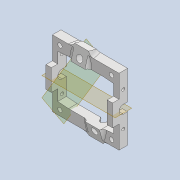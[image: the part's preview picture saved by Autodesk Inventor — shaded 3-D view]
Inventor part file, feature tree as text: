
AUTODESK INVENTOR PART (.ipt)
format: ipt  version: 2020 (Build 240168000, 168)  size: 697,856 bytes
history: native  units: mm
features: reference x17, projected_geometry x17, extrude x15, sketch x15, other x7, plane x4, fillet x4, thicken_offset x4, mirror x2, chamfer x2
ambient origin geometry x8: Origin, YZ Plane, XZ Plane, XY Plane, X Axis, Y Axis, Z Axis, Center Point
bodies: Solid1 (feature_tree)
feature tree (87):
  extrude  "Extrusion1"  Depth=21.0mm
  extrude  "Extrusion2"  Depth=2.5mm
  extrude  "Extrusion3"  Depth=4.0mm TaperAngle=0.0deg
  extrude  "Extrusion4"  Depth=10.0mm TaperAngle=0.0deg
  extrude  "Extrusion5"  Depth=10.0mm TaperAngle=0.0deg
  extrude  "Extrusion6"  Depth=4.0mm
  extrude  "Extrusion7"  Depth=10.0mm
  plane  "Work Plane1"
  sketch  "Sketch8"  dims[d19=10.0mm d20=50.0mm d21=0.0mm]
  plane  "Work Plane2"
  extrude  "Extrusion8"  Depth=10.0mm TaperAngle=0.0deg
  plane  "Work Plane3"
  mirror  "Mirror1"
  extrude  "Extrusion9"  Depth=14.0mm
  sketch  "Sketch10"  dims[d25=12.0mm d26=50.0mm d27=0.0mm]
  plane  "Work Plane4"
  extrude  "Extrusion11"  Depth=50.0mm TaperAngle=0.0deg
  mirror  "Mirror2"
  extrude  "Extrusion12"  Depth=24.0mm
  chamfer  "Chamfer1"  Distance=5.0mm
  fillet  "Fillet1"  Radius=5.0mm
  extrude  "Extrusion13"  Depth=0.4mm
  chamfer  "Chamfer2"  Distance=5.0mm
  fillet  "Fillet2"  Radius=0.4mm
  thicken_offset  "Thicken1"
  thicken_offset  "Thicken2"
  thicken_offset  "Thicken3"
  thicken_offset  "Thicken4"
  extrude  "Extrusion14"  Depth=4.0mm TaperAngle=0.0deg
  extrude  "Extrusion15"  Depth=2.5mm
  fillet  "Fillet3"  Radius=3.85mm
  fillet  "Fillet4"  Radius=2.5mm
  extrude  "Extrusion16"  Depth=3.0mm
  sketch  "Sketch1"  dims[d0=26.0mm d1=21.0mm]
  reference  "Reference1"
  reference  "Reference2"
  reference  "Reference3"
  reference  "Reference4"
  reference  "Reference5"
  reference  "Reference6"
  reference  "Reference7"
  reference  "Reference8"
  sketch  "Sketch2"  dims[d2=5.0mm d3=2.5mm]
  reference  "Reference9"
  reference  "Reference10"
  sketch  "Sketch3"  dims[d4=4.0mm d5=0.0mm d6=4.0mm d7=0.0mm]
  projected_geometry  "Projected Loop1"
  reference  "Reference11"
  sketch  "Sketch4"  dims[d8=10.0mm d9=4.0mm d10=0.0mm]
  reference  "Reference12"
  sketch  "Sketch5"  dims[d11=10.0mm d12=4.0mm d13=0.0mm]
  reference  "Reference13"
  sketch  "Sketch6"  dims[d14=5.0mm d15=4.0mm]
  projected_geometry  "Projected Loop2"
  sketch  "Sketch7"  dims[d16=50.0mm d17=0.0mm d18=10.0mm]
  projected_geometry  "Projected Loop3"
  projected_geometry  "Projected Loop4"
  projected_geometry  "Projected Loop5"
  reference  "Reference14"
  sketch  "Sketch9"  dims[d22=50.0mm d23=0.0mm d24=14.0mm]
  projected_geometry  "Projected Loop6"
  projected_geometry  "Projected Loop7"
  projected_geometry  "Projected Loop8"
  projected_geometry  "Projected Loop9"
  projected_geometry  "Projected Loop10"
  reference  "Reference15"
  projected_geometry  "Projected Loop11"
  sketch  "Sketch11"  dims[d28=26.0mm d29=24.0mm]
  reference  "Reference16"
  projected_geometry  "Projected Loop12"
  sketch  "Sketch12"  dims[d30=2.0mm]
  projected_geometry  "Projected Loop13"
  reference  "Reference17"
  sketch  "Sketch13"  dims[d31=2.0mm]
  projected_geometry  "Projected Loop14"
  sketch  "Sketch14"  dims[d32=2.0mm]
  projected_geometry  "Projected Loop15"
  sketch  "Sketch15"  dims[d33=2.0mm d34=5.0mm d35=0.0mm d37=5.0mm d38=0.4mm d39=5.0mm d42=0.4mm d43=4.0mm d44=0.0mm d45=2.5mm d46=3.85mm d47=2.5mm d48=3.0mm d49=7.0mm d50=0.0mm d51=0.5mm d52=2.0mm d53=45.0deg d54=0.2mm d55=2.5mm d56=3.85mm d57=3.0mm d58=7.0mm d59=0.0mm d60=0.5mm d61=2.0mm d62=45.0deg d63=0.2mm d64=8.25mm d65=9.0mm d66=6.0mm d67=6.0mm d68=1.5mm d69=1.5mm d70=0.75mm d71=0.75mm d72=6.5mm d73=1.5mm d74=7.0mm d75=0.0mm d76=6.5mm d77=1.5mm d78=7.0mm d79=0.0mm d80=3.0mm d81=2.0mm d82=5.0mm d83=5.0mm d84=1.4mm d85=1.4mm d86=7.0mm d87=0.0mm]
  projected_geometry  "Projected Loop16"
  projected_geometry  "Projected Loop17"
  parser-record x1  (decoder bookkeeping rows leaked as tree rows — omitted from the tree; the rows remain in map.json)
  other  "tip_3_n_ass.iam"
  other  "bearing_hh_1:2"
  other  "bearing_hh_1:1"
  other  "pin3_40:1"
  other  "roller_n_1:1"
  other  "roller_n_1:2"
note: 1 file-system path scrubbed to <path> (originals preserved in map.json)
